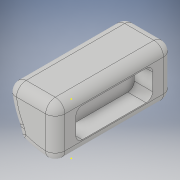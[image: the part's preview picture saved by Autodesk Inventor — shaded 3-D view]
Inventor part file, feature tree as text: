
AUTODESK INVENTOR PART (.ipt)
format: ipt  version: 2018 (Build 220112000, 112)  size: 199,168 bytes
history: native  units: in
note: dims shown in document units (in); Inventor stores cm internally (conversion verified against a paired STEP export)
features: sketch x4, fillet x4, extrude x2, plane x1
ambient origin geometry x8: Origin, YZ Plane, XZ Plane, XY Plane, X Axis, Y Axis, Z Axis, Center Point
bodies: Solid1 (feature_tree)
feature tree (11):
  sketch  "Sketch1"  dims[d8=1.53in d9=2.3in]
  extrude  "Extrusion1"  Depth=2.3in
  plane  "Work Plane1"
  extrude  "Extrusion2"  Depth=3.17in TaperAngle=0.0deg
  fillet  "Fillet1"  [1 undecoded]
  fillet  "Fillet2"  Radius=2.39in
  fillet  "Fillet3"  Radius=0.93in
  fillet  "Fillet4"  Radius=0.57in
  sketch  "Sketch4"  dims[d21=0.3in d22=0.3in d23=0.3in]
  sketch  "Sketch2"  dims[d10=2.356in d11=3.17in d12=0.5in d13=0.0in d14=0.0in d15=0.0in d16=2.39in d17=0.93in d18=0.57in d19=0.0in]
  sketch  "Sketch3"  dims[d20=0.2in]
note: 1 required parameter value undecoded (feature->parameter linkage not recoverable at this tier; creation-order binding heuristic only, values carry confidence <= 0.55)
